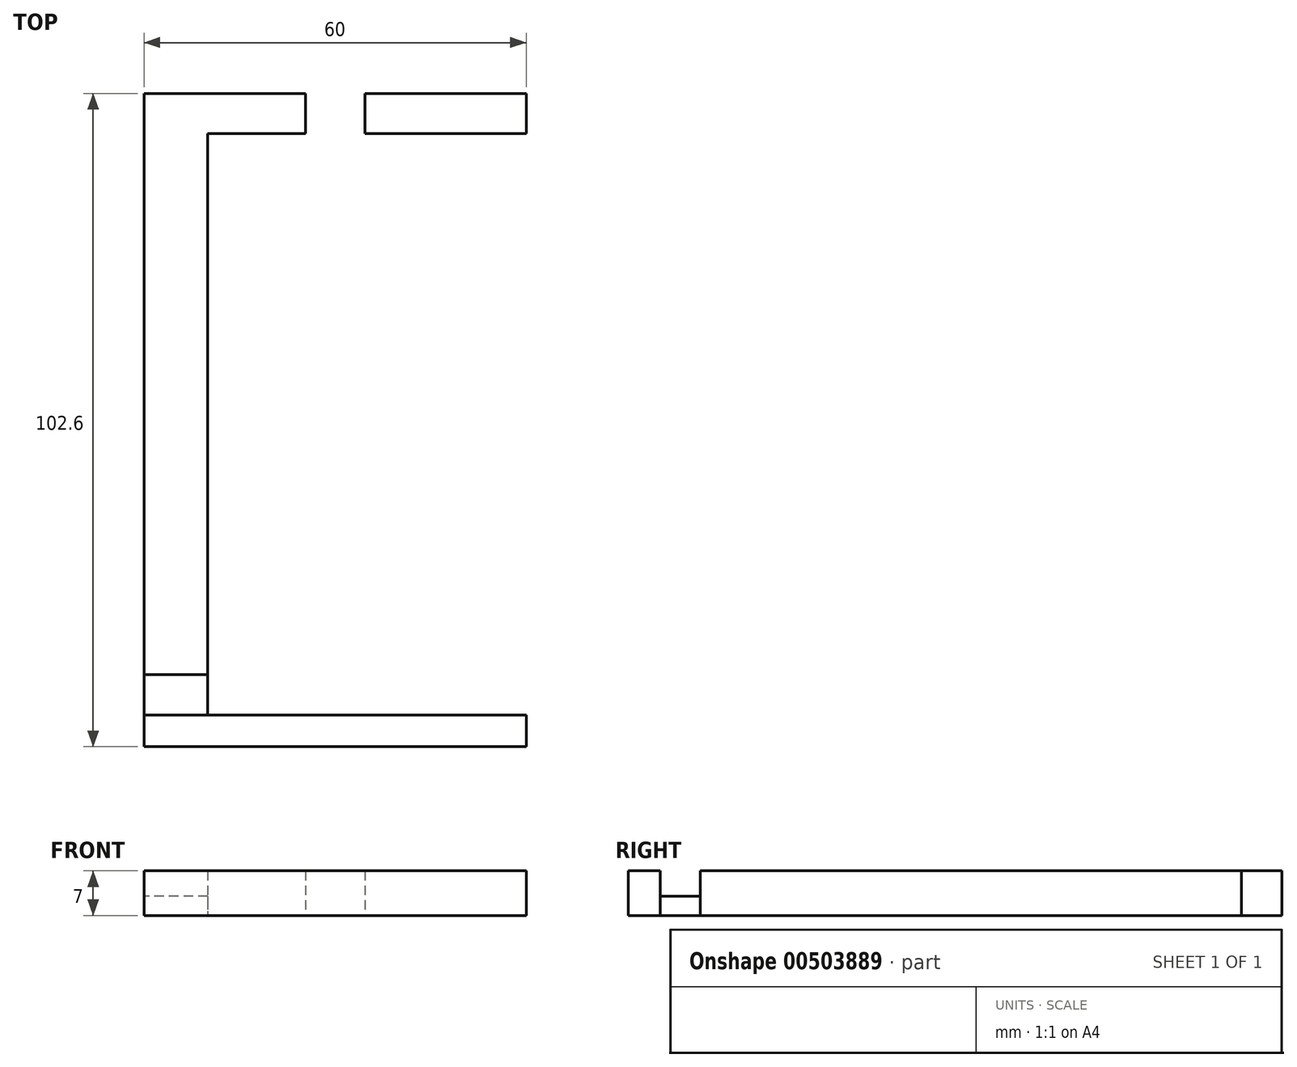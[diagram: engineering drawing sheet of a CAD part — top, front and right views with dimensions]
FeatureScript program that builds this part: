
annotation { "Feature Type Name" : "Feature", "Feature Type Description" : "" }
export const myFeature = defineFeature(function(context is Context, id is Id, definition is map)
    precondition{}
    {
        {
            var Q0;
            Q0=qCreatedBy(makeId("Top.planeOp"),FACE);
            var sketch = newSketch(context, id + "F0", { "sketchPlane" : qUnion([Q0])});
            skLineSegment(sketch, "E0.top", {"start": v(30, -51.3) * mm, "end": v(-30, -51.3) * mm});
            skLineSegment(sketch, "E0.left", {"start": v(30, 51.3) * mm, "end": v(30, -51.3) * mm});
            skLineSegment(sketch, "E0.right", {"start": v(-30, 51.3) * mm, "end": v(-30, -51.3) * mm});
            skPoint(sketch, "E0.middle", {"position": v(0, 0) * mm});
            skLineSegment(sketch, "E1", {"start": v(0, 0) * mm, "end": v(0, -40) * mm});
            skLineSegment(sketch, "E2", {"start": v(0, -40) * mm, "end": v(30, -40) * mm});
            skLineSegment(sketch, "E3", {"start": v(30, -40) * mm, "end": v(30, -46.3) * mm});
            skLineSegment(sketch, "E4", {"start": v(30, -46.3) * mm, "end": v(0, -46.3) * mm});
            skLineSegment(sketch, "E5.MirrorCS", {"start": v(0, -40) * mm, "end": v(-30, -40) * mm});
            skLineSegment(sketch, "E6.MirrorCS", {"start": v(-30, -46.3) * mm, "end": v(0, -46.3) * mm});
            skLineSegment(sketch, "E7", {"start": v(30, -40) * mm, "end": v(20, -40) * mm});
            skLineSegment(sketch, "E8", {"start": v(30, 45) * mm, "end": v(-30, 45) * mm});
            skLineSegment(sketch, "E9", {"start": v(20, -40) * mm, "end": v(20, 45) * mm});
            skLineSegment(sketch, "E10", {"start": v(20, -40) * mm, "end": v(20, -51.3) * mm});
            skLineSegment(sketch, "E11", {"start": v(0, 45) * mm, "end": v(4.65, 45) * mm});
            skLineSegment(sketch, "E12", {"start": v(4.65, 45) * mm, "end": v(4.65, 51.3) * mm});
            skLineSegment(sketch, "E13", {"start": v(4.65, 51.3) * mm, "end": v(30, 51.3) * mm});
            skLineSegment(sketch, "E14.MirrorCS", {"start": v(-4.65, 45) * mm, "end": v(-4.65, 51.3) * mm});
            skLineSegment(sketch, "E15.MirrorCS", {"start": v(-4.65, 51.3) * mm, "end": v(-30, 51.3) * mm});
            skLineSegment(sketch, "E16.MirrorCS", {"start": v(-20, -40) * mm, "end": v(-20, 45) * mm});
            skLineSegment(sketch, "E17.MirrorCS", {"start": v(-20, -40) * mm, "end": v(-20, -51.3) * mm});
            skLineSegment(sketch, "E18", {"start": v(4.65, 51.3) * mm, "end": v(4.65, 48.15) * mm});
            skLineSegment(sketch, "E19", {"start": v(4.65, 48.15) * mm, "end": v(-4.65, 48.15) * mm});
            skLineSegment(sketch, "E20", {"start": v(30, -46.3) * mm, "end": v(30, -51.3) * mm});
            skLineSegment(sketch, "E21", {"start": v(30, 51.3) * mm, "end": v(30, -40) * mm});
            skSolve(sketch);
        }
        {
            var Q0;
            {var subQ0=sQuery(id+"F0.wireOp",EDGE,"E7");Q0=makeQuery(id+"F0.imprint","IMPRINT",FACE,{"disambiguationData":[TD([[makeQuery(id+"F0.imprint","IMPRINT",EDGE,{"derivedFrom":subQ0}),-1.0]])]});}
            var Q1;
            {var subQ2=sQuery(id+"F0.wireOp",EDGE,"E12");Q1=makeQuery(id+"F0.imprint","IMPRINT",FACE,{"disambiguationData":[TD([[makeQuery(id+"F0.imprint","IMPRINT",EDGE,{"derivedFrom":subQ2}),-1.0]])]});}
            var Q2;
            {var subQ0=sQuery(id+"F0.wireOp",EDGE,"E14.MirrorCS");Q2=makeQuery(id+"F0.imprint","IMPRINT",FACE,{"disambiguationData":[TD([[makeQuery(id+"F0.imprint","IMPRINT",EDGE,{"derivedFrom":subQ0}),1.0]])]});}
            var Q3;
            {var subQ5=sQuery(id+"F0.wireOp",EDGE,"E16.MirrorCS");Q3=makeQuery(id+"F0.imprint","IMPRINT",FACE,{"disambiguationData":[TD([[makeQuery(id+"F0.imprint","IMPRINT",EDGE,{"derivedFrom":subQ5}),1.0]])]});}
            var Q4;
            {var subQ0=sQuery(id+"F0.wireOp",EDGE,"E0.right");var subQ1=sQuery(id+"F0.wireOp",EDGE,"E0.top");var subQ2=makeQuery(id+"F0.imprint","INTERSECT",VERTEX,{"derivedFrom":[subQ1,subQ0]});Q4=makeQuery(id+"F0.imprint","IMPRINT",FACE,{"disambiguationData":[TD([[makeQuery(id+"F0.imprint","IMPRINT",EDGE,{"disambiguationData":[TD([[subQ2,1.0]])],"derivedFrom":subQ1}),-1.0]])]});}
            var Q5;
            {var subQ5=sQuery(id+"F0.wireOp",EDGE,"E10");var subQ7=sQuery(id+"F0.wireOp",EDGE,"E0.top");var subQ8=makeQuery(id+"F0.imprint","INTERSECT",VERTEX,{"derivedFrom":[subQ7,subQ5]});Q5=makeQuery(id+"F0.imprint","IMPRINT",FACE,{"disambiguationData":[TD([[makeQuery(id+"F0.imprint","IMPRINT",EDGE,{"disambiguationData":[TD([[subQ8,-1.0]])],"derivedFrom":subQ7}),-1.0]])]});}
            var Q6;
            {var subQ0=sQuery(id+"F0.wireOp",EDGE,"E0.left");var subQ1=sQuery(id+"F0.wireOp",EDGE,"E0.top");var subQ2=makeQuery(id+"F0.imprint","INTERSECT",VERTEX,{"derivedFrom":[subQ1,subQ0]});Q6=makeQuery(id+"F0.imprint","IMPRINT",FACE,{"disambiguationData":[TD([[makeQuery(id+"F0.imprint","IMPRINT",EDGE,{"disambiguationData":[TD([[subQ2,-1.0]])],"derivedFrom":subQ1}),-1.0]])]});}
            var Q7;
            {var subQ4=sQuery(id+"F0.wireOp",EDGE,"E11");Q7=makeQuery(id+"F0.imprint","IMPRINT",FACE,{"disambiguationData":[TD([[makeQuery(id+"F0.imprint","IMPRINT",EDGE,{"derivedFrom":subQ4}),1.0]])]});}
            extrude(context, id + "F1", {"entities" : qUnion([Q0, Q1, Q2, Q3, Q4, Q5, Q6, Q7]), "depth" : 7 * mm, "offsetDistance" : 25 * mm});
        }
        {
            var Q0;
            {var subQ0=sQuery(id+"F0.wireOp",EDGE,"E3");Q0=makeQuery(id+"F0.imprint","IMPRINT",FACE,{"disambiguationData":[TD([[makeQuery(id+"F0.imprint","IMPRINT",EDGE,{"derivedFrom":subQ0}),-1.0]])]});}
            var Q1;
            {var subQ0=sQuery(id+"F0.wireOp",EDGE,"E5.MirrorCS");var subQ1=sQuery(id+"F0.wireOp",EDGE,"E0.right");var subQ2=makeQuery(id+"F0.imprint","INTERSECT",VERTEX,{"derivedFrom":[subQ1,subQ0]});Q1=makeQuery(id+"F0.imprint","IMPRINT",FACE,{"disambiguationData":[TD([[makeQuery(id+"F0.imprint","IMPRINT",EDGE,{"disambiguationData":[TD([[subQ2,-1.0]])],"derivedFrom":subQ1}),1.0]])]});}
            extrude(context, id + "F2", {"entities" : qUnion([Q0, Q1]), "depth" : 3 * mm, "offsetDistance" : 25 * mm});
        }
    });
